# Revit family: Bayville Spike Spot AC
name_source: partatom
category: Lighting Fixtures
revit_build: Autodesk Revit 2018 (Build: 20170223_1515(x64)
units: mm (PartAtom-declared; Revit-internal decimal feet)

## family parameters
Always vertical = Yes
Cut with Voids When Loaded = No
Light Source = Yes
OmniClass Number = 23.80.70.00
OmniClass Title = Lighting
Part Type = Normal
Room Calculation Point = No
Round Connector Dimension = Use Diameter
Shared = No
Work Plane-Based = No

## types (2) — shared parameters
Color Filter = 16777215
Dimmable = Yes
Dimming Lamp Color Temperature Shift = <None>
Dimming Method = Phase
Driver Required = No
Efficacy (lm/W) = 68
Electrical Class = 1
Emit from Line Length = 610 mm
Lamp = LED
Length of Cable Supplied = 1300
Location Rating = IP65
Main Material = Aluminium / Stainless steel Spike
Photometric Web File = GNC-21942 Bayville Single Spotlight - 1401005 [8306].ies
Power (W) = 7.6
Product Location = Ground
Product Name = Bayville Spike Spot
Tilt Angle = 60.00°

## per-type parameters (varying)
| type | Main Finish | Prdouct Code | Product SKU |
| Textured Black | Textured black | 8308 | 1401007 |
| Textured Grey | Textured Grey | 8309 | 1401008 |

## geometry (parser evidence)
native form markers: Sweep x3
no freeform markers — native parametric forms only
